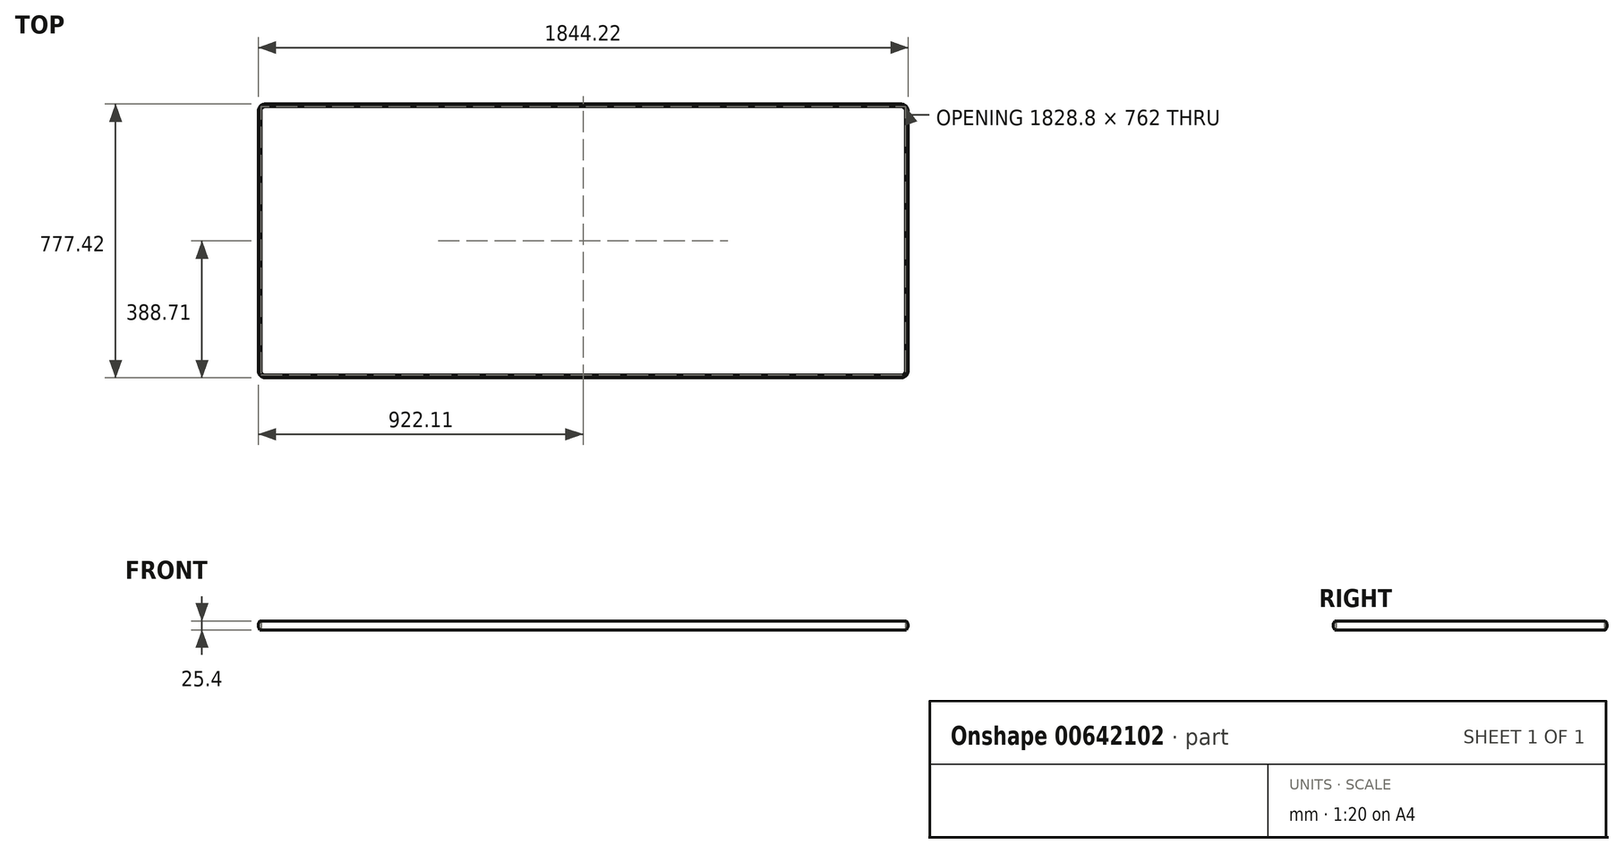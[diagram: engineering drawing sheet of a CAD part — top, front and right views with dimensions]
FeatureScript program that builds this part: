
annotation { "Feature Type Name" : "Feature", "Feature Type Description" : "" }
export const myFeature = defineFeature(function(context is Context, id is Id, definition is map)
    precondition{}
    {
        {
            var Q0;
            Q0=qCreatedBy(makeId("Top.planeOp"),FACE);
            var sketch = newSketch(context, id + "F0", { "sketchPlane" : qUnion([Q0])});
            skLineSegment(sketch, "E0.bottom", {"start": v(901.7, -381) * mm, "end": v(-901.7, -381) * mm});
            skLineSegment(sketch, "E0.top", {"start": v(901.7, 381) * mm, "end": v(-901.7, 381) * mm});
            skLineSegment(sketch, "E0.left", {"start": v(914.4, -368.3) * mm, "end": v(914.4, 368.3) * mm});
            skLineSegment(sketch, "E0.right", {"start": v(-914.4, -368.3) * mm, "end": v(-914.4, 368.3) * mm});
            skPoint(sketch, "E0.middle", {"position": v(0, 0) * mm});
            skPoint(sketch, "E1.visualSharp", {"position": v(-914.4, 381) * mm});
            skArc(sketch, "E1.filletArc", {"start": v(-901.7, 381) * mm, "mid": v(-910.68, 377.28) * mm, "end": v(-914.4, 368.3) * mm});
            skPoint(sketch, "E2.visualSharp", {"position": v(-914.4, -381) * mm});
            skArc(sketch, "E2.filletArc", {"start": v(-914.4, -368.3) * mm, "mid": v(-910.68, -377.28) * mm, "end": v(-901.7, -381) * mm});
            skPoint(sketch, "E3.visualSharp", {"position": v(914.4, -381) * mm});
            skArc(sketch, "E3.filletArc", {"start": v(901.7, -381) * mm, "mid": v(910.68, -377.28) * mm, "end": v(914.4, -368.3) * mm});
            skPoint(sketch, "E4.visualSharp", {"position": v(914.4, 381) * mm});
            skArc(sketch, "E4.filletArc", {"start": v(914.4, 368.3) * mm, "mid": v(910.68, 377.28) * mm, "end": v(901.7, 381) * mm});
            skLineSegment(sketch, "E5.bottom", {"start": v(902.34, 384.18) * mm, "end": v(-902.34, 384.17) * mm});
            skLineSegment(sketch, "E5.top", {"start": v(902.34, -384.17) * mm, "end": v(-902.34, -384.18) * mm});
            skLineSegment(sketch, "E5.left", {"start": v(917.58, 368.94) * mm, "end": v(917.58, -368.93) * mm});
            skLineSegment(sketch, "E5.right", {"start": v(-917.58, 368.94) * mm, "end": v(-917.58, -368.94) * mm});
            skPoint(sketch, "E6.visualSharp", {"position": v(917.58, 384.18) * mm});
            skArc(sketch, "E6.filletArc", {"start": v(917.58, 368.94) * mm, "mid": v(913.11, 379.71) * mm, "end": v(902.34, 384.18) * mm});
            skPoint(sketch, "E7.visualSharp", {"position": v(917.58, -384.17) * mm});
            skArc(sketch, "E7.filletArc", {"start": v(902.34, -384.17) * mm, "mid": v(913.11, -379.71) * mm, "end": v(917.58, -368.93) * mm});
            skPoint(sketch, "E8.visualSharp", {"position": v(-917.58, -384.18) * mm});
            skArc(sketch, "E8.filletArc", {"start": v(-917.58, -368.94) * mm, "mid": v(-913.11, -379.71) * mm, "end": v(-902.34, -384.18) * mm});
            skPoint(sketch, "E9.visualSharp", {"position": v(-917.58, 384.17) * mm});
            skArc(sketch, "E9.filletArc", {"start": v(-902.34, 384.17) * mm, "mid": v(-913.11, 379.71) * mm, "end": v(-917.58, 368.94) * mm});
            skSolve(sketch);
        }
        {
            var Q0;
            Q0=makeQuery(id+"F0.imprint","IMPRINT",FACE,{"disambiguationData":[TD([[makeQuery(id+"F0.imprint","IMPRINT",EDGE,{"derivedFrom":sQuery(id+"F0.wireOp",EDGE,"E0.bottom")}),1.0]])]});
            extrude(context, id + "F1", {"entities" : qUnion([Q0]), "depth" : 25.4 * mm, "offsetDistance" : 25.4 * mm});
        }
        {
            var Q0;
            Q0=makeQuery(id+"F1.opExtrude","SWEPT_FACE",FACE,{"disambiguationData":[OSD([sQuery(id+"F0.wireOp",EDGE,"E5.top")])]});
            var sketch = newSketch(context, id + "F2", { "sketchPlane" : qUnion([Q0])});
            skLineSegment(sketch, "E10.bottom", {"start": v(902.34, 25.4) * mm, "end": v(-902.34, 25.4) * mm});
            skLineSegment(sketch, "E10.top", {"start": v(902.34, 0) * mm, "end": v(-902.34, 0) * mm});
            skLineSegment(sketch, "E10.left", {"start": v(902.34, 25.4) * mm, "end": v(902.34, 0) * mm});
            skLineSegment(sketch, "E10.right", {"start": v(-902.34, 25.4) * mm, "end": v(-902.34, 0) * mm});
            skSolve(sketch);
        }
        {
            var Q0;
            Q0 = qSketchRegion(id + "F2", true);
            extrude(context, id + "F3", {"entities" : qUnion([Q0]), "operationType" : NewBodyOperationType.ADD, "depth" : 6.35 * mm, "offsetDistance" : 25.4 * mm});
        }
        {
            var Q0;
            Q0=makeQuery(id+"F3.opExtrude","SWEPT_FACE",FACE,{"disambiguationData":[OSD([sQuery(id+"F2.wireOp",EDGE,"E10.right")])]});
            var sketch = newSketch(context, id + "F4", { "sketchPlane" : qUnion([Q0])});
            skArc(sketch, "E11", {"start": v(384.18, 0) * mm, "mid": v(388.7, 12.7) * mm, "end": v(384.18, 25.4) * mm});
            skLineSegment(sketch, "E12", {"start": v(384.18, 25.4) * mm, "end": v(384.18, 0) * mm});
            skLineSegment(sketch, "E13", {"start": v(384.18, 25.4) * mm, "end": v(390.53, 25.4) * mm});
            skLineSegment(sketch, "E14", {"start": v(390.53, 25.4) * mm, "end": v(390.53, 0) * mm});
            skLineSegment(sketch, "E15", {"start": v(390.53, 0) * mm, "end": v(384.18, 0) * mm});
            skSolve(sketch);
        }
        {
            var Q0;
            Q0=makeQuery(id+"F4.imprint","IMPRINT",FACE,{"disambiguationData":[TD([[makeQuery(id+"F4.imprint","IMPRINT",EDGE,{"derivedFrom":sQuery(id+"F4.wireOp",EDGE,"E11")}),-1.0]])]});
            extrude(context, id + "F5", {"entities" : qUnion([Q0]), "operationType" : NewBodyOperationType.REMOVE, "oppositeDirection" : true, "depth" : 2540 * mm, "offsetDistance" : 25.4 * mm});
        }
        {
            var Q0;
            Q0=makeQuery(id+"F3.opExtrude","SWEPT_FACE",FACE,{"disambiguationData":[OSD([sQuery(id+"F2.wireOp",EDGE,"E10.right")])]});
            var Q1;
            Q1=makeQuery(id+"F1.opExtrude","CAP_EDGE",EDGE,{"disambiguationData":[OSD([sQuery(id+"F0.wireOp",EDGE,"E8.filletArc")])],"isStart":false});
            var Q2;
            Q2=makeQuery(id+"F5.boolean.opBoolean","COPY",EDGE,{"derivedFrom":makeQuery(id+"F5.opExtrude","SWEPT_EDGE",EDGE,{"disambiguationData":[OSD([sQuery(id+"F4.wireOp",EDGE,"E11"),sQuery(id+"F4.wireOp",EDGE,"E12"),sQuery(id+"F4.wireOp",EDGE,"E13")])]})});
            var Q3;
            Q3=makeQuery(id+"F1.opExtrude","CAP_EDGE",EDGE,{"disambiguationData":[OSD([sQuery(id+"F0.wireOp",EDGE,"E5.right")])],"isStart":false});
            var Q4;
            Q4=makeQuery(id+"F1.opExtrude","CAP_EDGE",EDGE,{"disambiguationData":[OSD([sQuery(id+"F0.wireOp",EDGE,"E9.filletArc")])],"isStart":false});
            var Q5;
            Q5=makeQuery(id+"F1.opExtrude","CAP_EDGE",EDGE,{"disambiguationData":[OSD([sQuery(id+"F0.wireOp",EDGE,"E5.bottom")])],"isStart":false});
            var Q6;
            Q6=makeQuery(id+"F1.opExtrude","CAP_EDGE",EDGE,{"disambiguationData":[OSD([sQuery(id+"F0.wireOp",EDGE,"E6.filletArc")])],"isStart":false});
            var Q7;
            Q7=makeQuery(id+"F1.opExtrude","CAP_EDGE",EDGE,{"disambiguationData":[OSD([sQuery(id+"F0.wireOp",EDGE,"E5.left")])],"isStart":false});
            var Q8;
            Q8=makeQuery(id+"F1.opExtrude","CAP_EDGE",EDGE,{"disambiguationData":[OSD([sQuery(id+"F0.wireOp",EDGE,"E7.filletArc")])],"isStart":false});
            sweep(context, id + "F6", {"operationType" : NewBodyOperationType.ADD, "profiles" : qUnion([Q0]), "path" : qUnion([Q1, Q2, Q3, Q4, Q5, Q6, Q7, Q8])});
        }
    });
